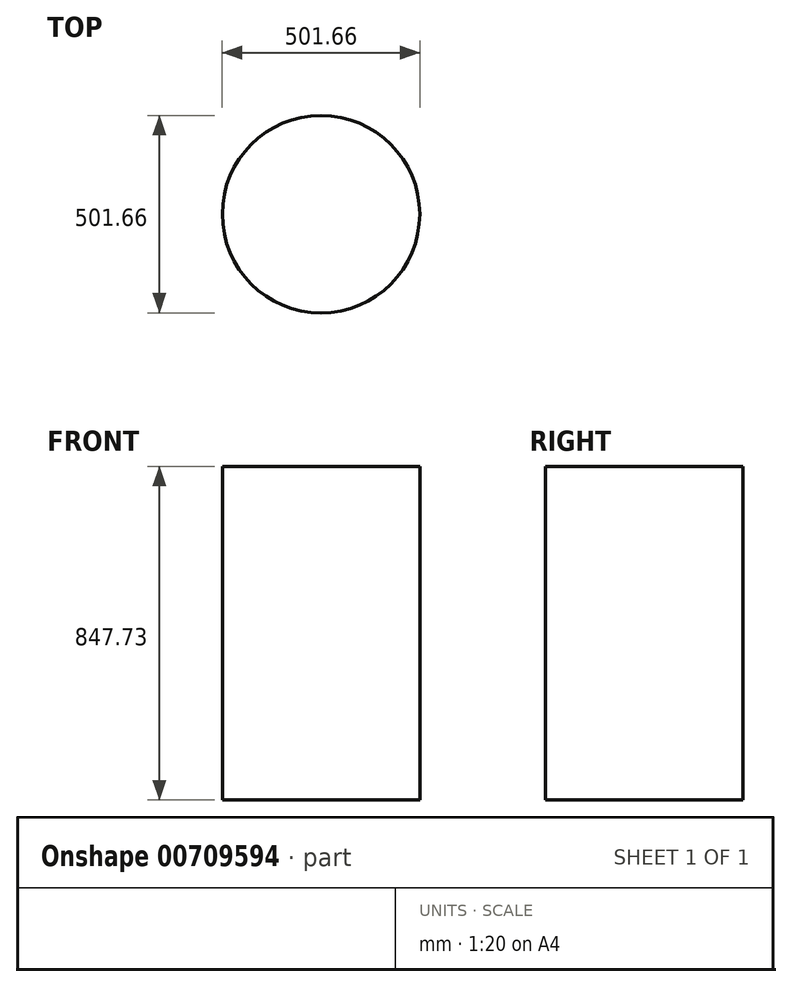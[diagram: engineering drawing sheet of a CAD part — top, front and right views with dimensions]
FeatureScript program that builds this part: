
annotation { "Feature Type Name" : "Feature", "Feature Type Description" : "" }
export const myFeature = defineFeature(function(context is Context, id is Id, definition is map)
    precondition{}
    {
        {
            var Q0;
            Q0=qCreatedBy(makeId("Top.planeOp"),FACE);
            var sketch = newSketch(context, id + "F0", { "sketchPlane" : qUnion([Q0])});
            skCircle(sketch, "E0", {"center": v(0, 0) * mm, "radius": 250.82 * mm});
            skSolve(sketch);
        }
        {
            var Q0;
            Q0=makeQuery(id+"F0.imprint","IMPRINT",FACE,{"disambiguationData":[TD([[makeQuery(id+"F0.imprint","IMPRINT",EDGE,{"derivedFrom":sQuery(id+"F0.wireOp",EDGE,"E0")}),1.0]])]});
            extrude(context, id + "F1", {"entities" : qUnion([Q0]), "depth" : 847.72 * mm, "offsetDistance" : 25.4 * mm});
        }
    });
